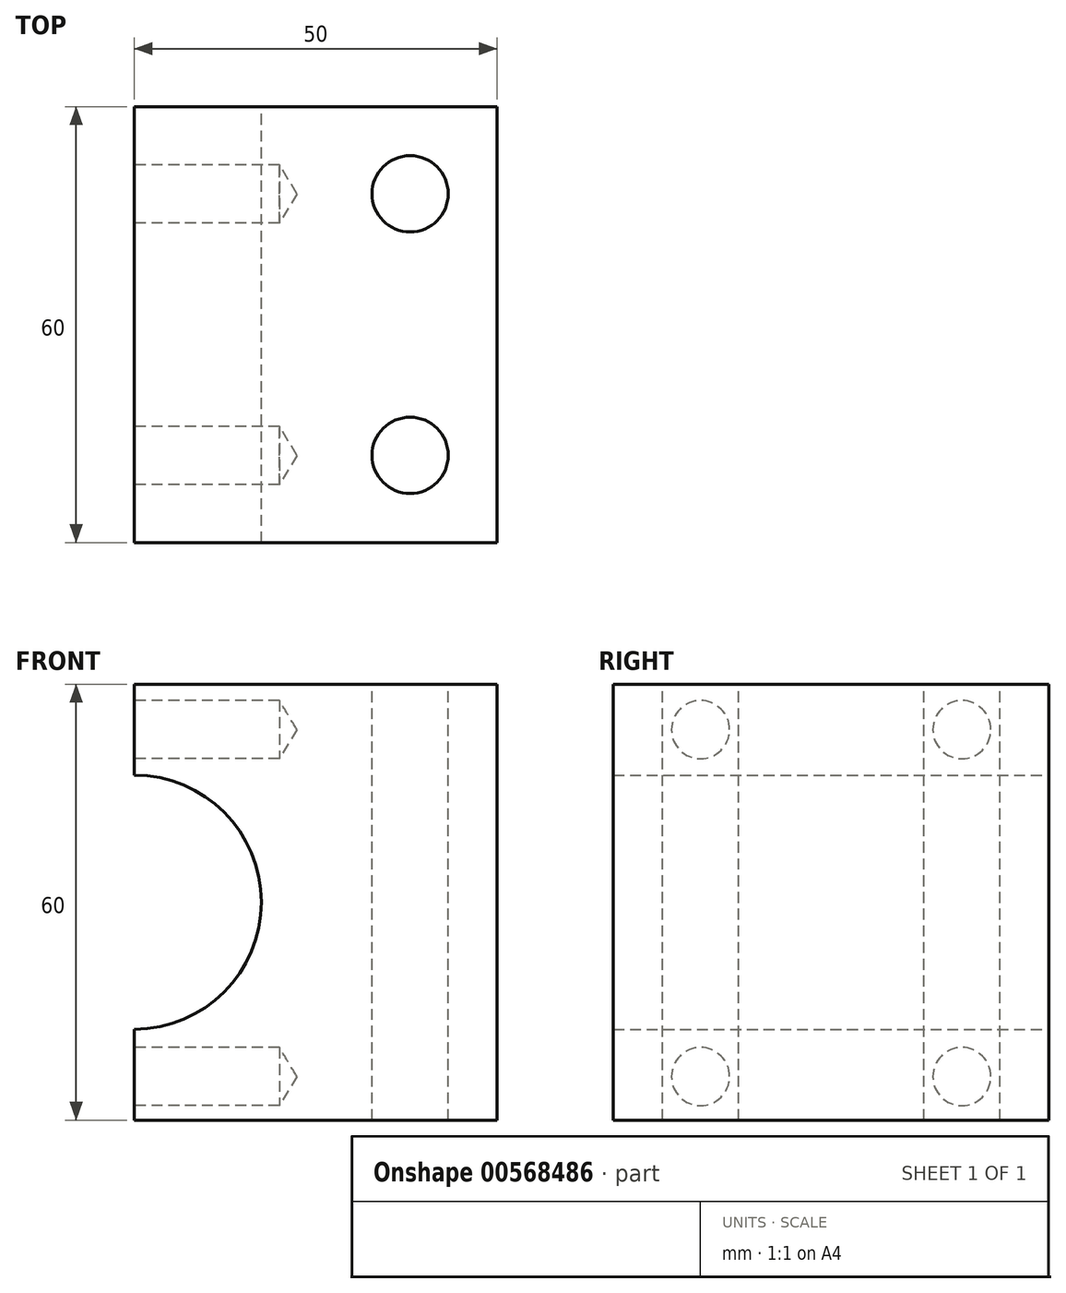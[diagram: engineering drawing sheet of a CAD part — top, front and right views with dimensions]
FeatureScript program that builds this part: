
annotation { "Feature Type Name" : "Feature", "Feature Type Description" : "" }
export const myFeature = defineFeature(function(context is Context, id is Id, definition is map)
    precondition{}
    {
        {
            var Q0;
            Q0=qCreatedBy(makeId("Front.planeOp"),FACE);
            var sketch = newSketch(context, id + "F0", { "sketchPlane" : qUnion([Q0])});
            skLineSegment(sketch, "E0.bottom", {"start": v(-25, -30) * mm, "end": v(25, -30) * mm});
            skLineSegment(sketch, "E0.top", {"start": v(-25, 30) * mm, "end": v(25, 30) * mm});
            skLineSegment(sketch, "E0.left", {"start": v(-25, -30) * mm, "end": v(-25, -17.5) * mm});
            skLineSegment(sketch, "E0.right", {"start": v(25, -30) * mm, "end": v(25, 30) * mm});
            skArc(sketch, "E1", {"start": v(-25, -17.5) * mm, "mid": v(-7.5, 0) * mm, "end": v(-25, 17.5) * mm});
            skLineSegment(sketch, "E2.trimOffspring", {"start": v(-25, 17.5) * mm, "end": v(-25, 30) * mm});
            skSolve(sketch);
        }
        {
            var Q0;
            Q0=makeQuery(id+"F0.imprint","IMPRINT",FACE,{"disambiguationData":[TD([[makeQuery(id+"F0.imprint","IMPRINT",EDGE,{"derivedFrom":sQuery(id+"F0.wireOp",EDGE,"E0.bottom")}),1.0]])]});
            extrude(context, id + "F1", {"entities" : qUnion([Q0]), "endBound" : BoundingType.SYMMETRIC, "depth" : 60 * mm, "offsetDistance" : 25 * mm});
        }
        {
            var Q0;
            Q0=makeQuery(id+"F1.opExtrude","SWEPT_FACE",FACE,{"disambiguationData":[OSD([sQuery(id+"F0.wireOp",EDGE,"E0.top")])]});
            var sketch = newSketch(context, id + "F2", { "sketchPlane" : qUnion([Q0])});
            skPoint(sketch, "E3", {"position": v(13, 18) * mm});
            skPoint(sketch, "E4", {"position": v(13, -18) * mm});
            skSolve(sketch);
        }
        {
            var Q0;
            Q0=sQuery(id+"F2.wireOp",VERTEX,"E3");
            var Q1;
            Q1=makeQuery(id+"F1.opExtrude","SWEPT_BODY",BODY,{"disambiguationData":[OSD([sQuery(id+"F0.wireOp",EDGE,"E0.bottom"),sQuery(id+"F0.wireOp",EDGE,"E0.top"),sQuery(id+"F0.wireOp",EDGE,"E0.left"),sQuery(id+"F0.wireOp",EDGE,"E0.right"),sQuery(id+"F0.wireOp",EDGE,"E1"),sQuery(id+"F0.wireOp",EDGE,"E2.trimOffspring")])]});
            hole(context, id + "F3", {"style" : HoleStyle.SIMPLE, "endStyle" : HoleEndStyle.THROUGH, "holeDiameter" : 10.5 * mm, "isTappedThrough" : true, "tappedDepth" : 12 * mm, "tapClearance" : 3, "locations" : qUnion([Q0]), "scope" : qUnion([Q1]), "majorDiameter" : 5 * mm});
        }
        {
            var Q0;
            Q0=sQuery(id+"F2.wireOp",VERTEX,"E4");
            var Q1;
            Q1=makeQuery(id+"F1.opExtrude","SWEPT_BODY",BODY,{"disambiguationData":[OSD([sQuery(id+"F0.wireOp",EDGE,"E0.bottom"),sQuery(id+"F0.wireOp",EDGE,"E0.top"),sQuery(id+"F0.wireOp",EDGE,"E0.left"),sQuery(id+"F0.wireOp",EDGE,"E0.right"),sQuery(id+"F0.wireOp",EDGE,"E1"),sQuery(id+"F0.wireOp",EDGE,"E2.trimOffspring")])]});
            hole(context, id + "F4", {"style" : HoleStyle.SIMPLE, "endStyle" : HoleEndStyle.THROUGH, "holeDiameter" : 10.5 * mm, "isTappedThrough" : true, "tappedDepth" : 12 * mm, "tapClearance" : 3, "locations" : qUnion([Q0]), "scope" : qUnion([Q1]), "majorDiameter" : 5 * mm});
        }
        {
            var Q0;
            Q0=makeQuery(id+"F1.opExtrude","SWEPT_FACE",FACE,{"disambiguationData":[OSD([sQuery(id+"F0.wireOp",EDGE,"E2.trimOffspring")])]});
            var sketch = newSketch(context, id + "F5", { "sketchPlane" : qUnion([Q0])});
            skPoint(sketch, "E5", {"position": v(-18, 23.75) * mm});
            skLineSegment(sketch, "E6", {"start": v(-30, 23.75) * mm, "end": v(30, 23.75) * mm});
            skPoint(sketch, "E7", {"position": v(18, 23.75) * mm});
            skLineSegment(sketch, "E8", {"start": v(-29.94, -24) * mm, "end": v(29.86, -24) * mm});
            skLineSegment(sketch, "E9", {"start": v(18, 23.75) * mm, "end": v(18, -24) * mm, "construction": true});
            skLineSegment(sketch, "E10", {"start": v(-18, 23.75) * mm, "end": v(-18, -24) * mm, "construction": true});
            skPoint(sketch, "E11", {"position": v(-18, -24) * mm});
            skPoint(sketch, "E12", {"position": v(18, -24) * mm});
            skSolve(sketch);
        }
        {
            var Q0;
            Q0=sQuery(id+"F5.wireOp",VERTEX,"E7");
            var Q1;
            Q1=sQuery(id+"F5.wireOp",VERTEX,"E5");
            var Q2;
            Q2=sQuery(id+"F5.wireOp",VERTEX,"E11");
            var Q3;
            Q3=sQuery(id+"F5.wireOp",VERTEX,"E12");
            var Q4;
            Q4=makeQuery(id+"F1.opExtrude","SWEPT_BODY",BODY,{"disambiguationData":[OSD([sQuery(id+"F0.wireOp",EDGE,"E0.bottom"),sQuery(id+"F0.wireOp",EDGE,"E0.top"),sQuery(id+"F0.wireOp",EDGE,"E0.left"),sQuery(id+"F0.wireOp",EDGE,"E0.right"),sQuery(id+"F0.wireOp",EDGE,"E1"),sQuery(id+"F0.wireOp",EDGE,"E2.trimOffspring")])]});
            hole(context, id + "F6", {"style" : HoleStyle.SIMPLE, "endStyle" : HoleEndStyle.BLIND, "holeDiameter" : 8 * mm, "holeDepth" : 20 * mm, "isTappedThrough" : true, "tappedDepth" : 12 * mm, "tapClearance" : 3, "locations" : qUnion([Q0, Q1, Q2, Q3]), "scope" : qUnion([Q4]), "majorDiameter" : 5 * mm});
        }
    });
